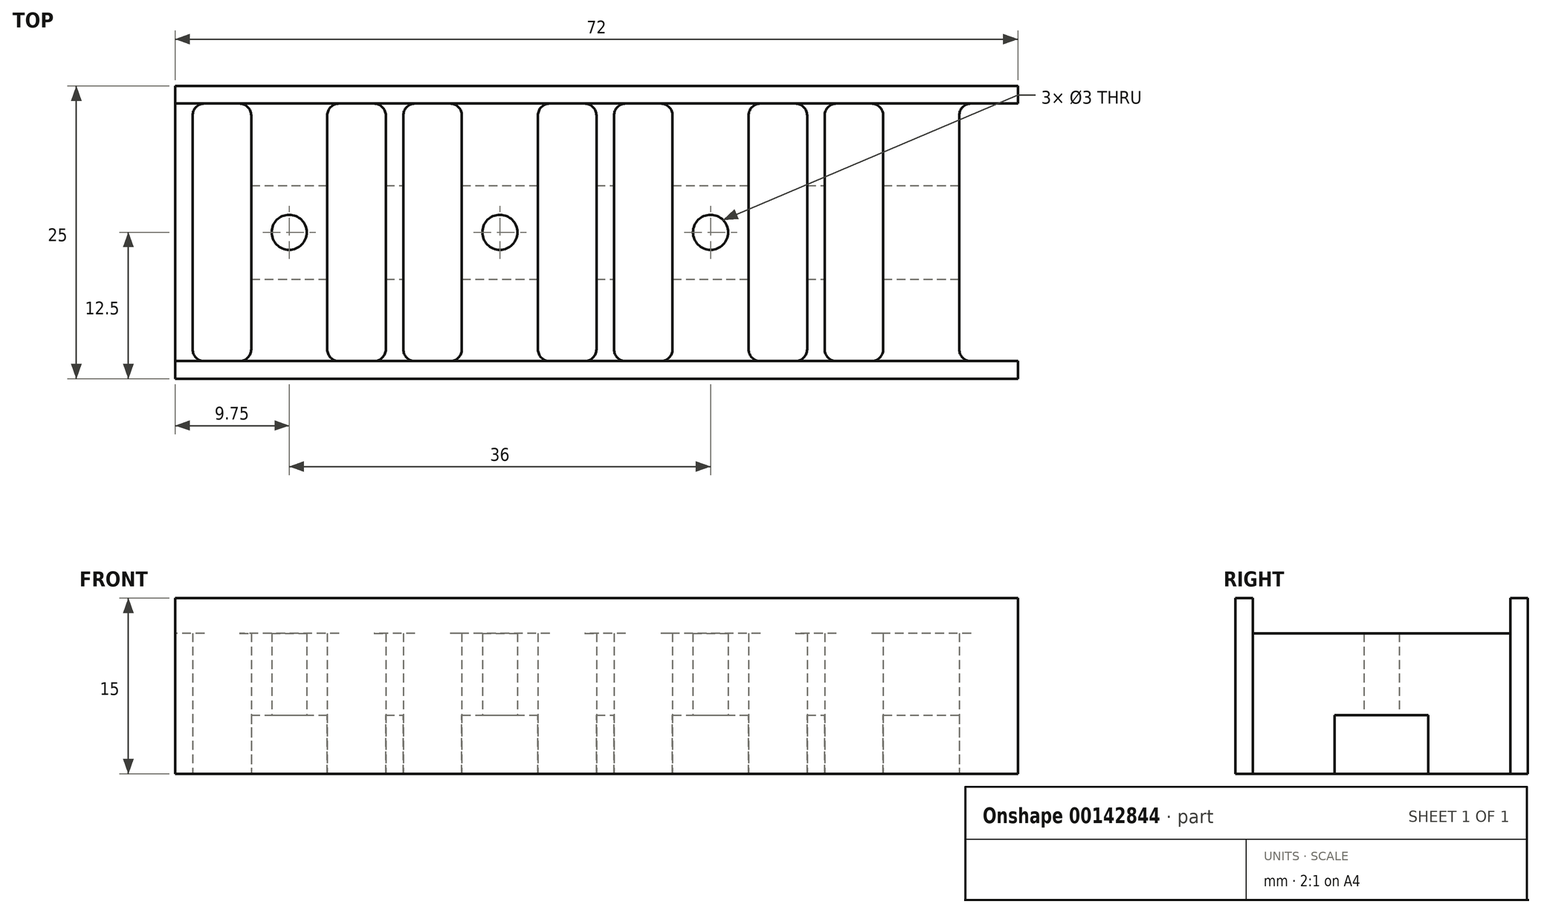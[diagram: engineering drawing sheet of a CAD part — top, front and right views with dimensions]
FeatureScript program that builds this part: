
annotation { "Feature Type Name" : "Feature", "Feature Type Description" : "" }
export const myFeature = defineFeature(function(context is Context, id is Id, definition is map)
    precondition{}
    {
        {
            var Q0;
            Q0=qCreatedBy(makeId("Top.planeOp"),FACE);
            var sketch = newSketch(context, id + "F0", { "sketchPlane" : qUnion([Q0])});
            skLineSegment(sketch, "E0.bottom", {"start": v(0, 12.5) * mm, "end": v(18, 12.5) * mm});
            skLineSegment(sketch, "E0.top", {"start": v(0, -12.5) * mm, "end": v(18, -12.5) * mm});
            skLineSegment(sketch, "E0.left", {"start": v(0, 12.5) * mm, "end": v(0, -12.5) * mm});
            skLineSegment(sketch, "E0.right", {"start": v(18, 12.5) * mm, "end": v(18, 11) * mm});
            skLineSegment(sketch, "E1.bottom", {"start": v(14, 11) * mm, "end": v(18, 11) * mm});
            skLineSegment(sketch, "E1.top", {"start": v(14, -11) * mm, "end": v(18, -11) * mm});
            skLineSegment(sketch, "E1.left", {"start": v(13, 10) * mm, "end": v(13, -10) * mm});
            skLineSegment(sketch, "E2.trimOffspring", {"start": v(18, -11) * mm, "end": v(18, -12.5) * mm});
            skLineSegment(sketch, "E3.bottom", {"start": v(2.5, 11) * mm, "end": v(5.5, 11) * mm});
            skLineSegment(sketch, "E3.top", {"start": v(2.5, -11) * mm, "end": v(5.5, -11) * mm});
            skLineSegment(sketch, "E3.left", {"start": v(1.5, 10) * mm, "end": v(1.5, -10) * mm});
            skLineSegment(sketch, "E3.right", {"start": v(6.5, 10) * mm, "end": v(6.5, -10) * mm});
            skCircle(sketch, "E4", {"center": v(9.75, 0) * mm, "radius": 1.5 * mm});
            skPoint(sketch, "E5.visualSharp", {"position": v(7.25, 11) * mm});
            skPoint(sketch, "E6.visualSharp", {"position": v(12.25, 11) * mm});
            skPoint(sketch, "E7.visualSharp", {"position": v(12.25, 3) * mm});
            skPoint(sketch, "E8.visualSharp", {"position": v(7.25, 3) * mm});
            skPoint(sketch, "E9.visualSharp", {"position": v(7.25, -3) * mm});
            skPoint(sketch, "E10.visualSharp", {"position": v(7.25, -11) * mm});
            skPoint(sketch, "E11.visualSharp", {"position": v(12.25, -11) * mm});
            skPoint(sketch, "E12.visualSharp", {"position": v(12.25, -3) * mm});
            skPoint(sketch, "E13.visualSharp", {"position": v(13, 11) * mm});
            skArc(sketch, "E13.filletArc", {"start": v(14, 11) * mm, "mid": v(13.3, 10.7) * mm, "end": v(13, 10) * mm});
            skPoint(sketch, "E14.visualSharp", {"position": v(13, -11) * mm});
            skArc(sketch, "E14.filletArc", {"start": v(13, -10) * mm, "mid": v(13.3, -10.7) * mm, "end": v(14, -11) * mm});
            skPoint(sketch, "E15.visualSharp", {"position": v(6.5, 11) * mm});
            skArc(sketch, "E15.filletArc", {"start": v(6.5, 10) * mm, "mid": v(6.2, 10.7) * mm, "end": v(5.5, 11) * mm});
            skPoint(sketch, "E16.visualSharp", {"position": v(6.5, -11) * mm});
            skArc(sketch, "E16.filletArc", {"start": v(5.5, -11) * mm, "mid": v(6.2, -10.7) * mm, "end": v(6.5, -10) * mm});
            skPoint(sketch, "E17.visualSharp", {"position": v(1.5, 11) * mm});
            skArc(sketch, "E17.filletArc", {"start": v(2.5, 11) * mm, "mid": v(1.8, 10.7) * mm, "end": v(1.5, 10) * mm});
            skPoint(sketch, "E18.visualSharp", {"position": v(1.5, -11) * mm});
            skArc(sketch, "E18.filletArc", {"start": v(1.5, -10) * mm, "mid": v(1.8, -10.7) * mm, "end": v(2.5, -11) * mm});
            skPoint(sketch, "E19.1.0.0", {"position": v(30.25, 3) * mm});
            skPoint(sketch, "E19.1.0.1", {"position": v(24.5, 11) * mm});
            skPoint(sketch, "E19.1.0.3", {"position": v(25.25, -11) * mm});
            skPoint(sketch, "E19.1.0.4", {"position": v(19.5, -11) * mm});
            skPoint(sketch, "E19.1.0.6", {"position": v(30.25, -11) * mm});
            skPoint(sketch, "E19.1.0.7", {"position": v(31, 11) * mm});
            skPoint(sketch, "E19.1.0.8", {"position": v(25.25, 11) * mm});
            skPoint(sketch, "E19.1.0.9", {"position": v(30.25, 11) * mm});
            skPoint(sketch, "E19.1.0.10", {"position": v(31, -11) * mm});
            skPoint(sketch, "E19.1.0.12", {"position": v(25.25, 3) * mm});
            skPoint(sketch, "E19.1.0.13", {"position": v(24.5, -11) * mm});
            skCircle(sketch, "E19.1.0.15", {"center": v(27.75, 0) * mm, "radius": 1.5 * mm});
            skLineSegment(sketch, "E19.1.0.16", {"start": v(24.5, 10) * mm, "end": v(24.5, -10) * mm});
            skLineSegment(sketch, "E19.1.0.17", {"start": v(19.5, 10) * mm, "end": v(19.5, -10) * mm});
            skLineSegment(sketch, "E19.1.0.18", {"start": v(20.5, -11) * mm, "end": v(23.5, -11) * mm});
            skLineSegment(sketch, "E19.1.0.19", {"start": v(20.5, 11) * mm, "end": v(23.5, 11) * mm});
            skLineSegment(sketch, "E19.1.0.20", {"start": v(31, 10) * mm, "end": v(31, -10) * mm});
            skLineSegment(sketch, "E19.1.0.21", {"start": v(32, -11) * mm, "end": v(36, -11) * mm});
            skLineSegment(sketch, "E19.1.0.22", {"start": v(32, 11) * mm, "end": v(36, 11) * mm});
            skPoint(sketch, "E19.1.0.23", {"position": v(25.25, -3) * mm});
            skPoint(sketch, "E19.1.0.24", {"position": v(19.5, 11) * mm});
            skLineSegment(sketch, "E19.1.0.25", {"start": v(18, 12.5) * mm, "end": v(18, -12.5) * mm});
            skLineSegment(sketch, "E19.1.0.26", {"start": v(18, -12.5) * mm, "end": v(36, -12.5) * mm});
            skLineSegment(sketch, "E19.1.0.27", {"start": v(18, 12.5) * mm, "end": v(36, 12.5) * mm});
            skPoint(sketch, "E19.1.0.32", {"position": v(30.25, -3) * mm});
            skArc(sketch, "E19.1.0.33", {"start": v(19.5, -10) * mm, "mid": v(19.8, -10.7) * mm, "end": v(20.5, -11) * mm});
            skArc(sketch, "E19.1.0.37", {"start": v(23.5, -11) * mm, "mid": v(24.2, -10.7) * mm, "end": v(24.5, -10) * mm});
            skArc(sketch, "E19.1.0.40", {"start": v(24.5, 10) * mm, "mid": v(24.2, 10.7) * mm, "end": v(23.5, 11) * mm});
            skArc(sketch, "E19.1.0.42", {"start": v(20.5, 11) * mm, "mid": v(19.8, 10.7) * mm, "end": v(19.5, 10) * mm});
            skArc(sketch, "E19.1.0.43", {"start": v(31, -10) * mm, "mid": v(31.3, -10.7) * mm, "end": v(32, -11) * mm});
            skArc(sketch, "E19.1.0.45", {"start": v(32, 11) * mm, "mid": v(31.3, 10.7) * mm, "end": v(31, 10) * mm});
            skLineSegment(sketch, "E19.1.0.47", {"start": v(36, -11) * mm, "end": v(36, -12.5) * mm});
            skLineSegment(sketch, "E19.1.0.48", {"start": v(36, 12.5) * mm, "end": v(36, 11) * mm});
            skPoint(sketch, "E19.2.0.0", {"position": v(48.25, 3) * mm});
            skPoint(sketch, "E19.2.0.1", {"position": v(42.5, 11) * mm});
            skPoint(sketch, "E19.2.0.3", {"position": v(43.25, -11) * mm});
            skPoint(sketch, "E19.2.0.4", {"position": v(37.5, -11) * mm});
            skPoint(sketch, "E19.2.0.6", {"position": v(48.25, -11) * mm});
            skPoint(sketch, "E19.2.0.7", {"position": v(49, 11) * mm});
            skPoint(sketch, "E19.2.0.8", {"position": v(43.25, 11) * mm});
            skPoint(sketch, "E19.2.0.9", {"position": v(48.25, 11) * mm});
            skPoint(sketch, "E19.2.0.10", {"position": v(49, -11) * mm});
            skPoint(sketch, "E19.2.0.12", {"position": v(43.25, 3) * mm});
            skPoint(sketch, "E19.2.0.13", {"position": v(42.5, -11) * mm});
            skCircle(sketch, "E19.2.0.15", {"center": v(45.75, 0) * mm, "radius": 1.5 * mm});
            skLineSegment(sketch, "E19.2.0.16", {"start": v(42.5, 10) * mm, "end": v(42.5, -10) * mm});
            skLineSegment(sketch, "E19.2.0.17", {"start": v(37.5, 10) * mm, "end": v(37.5, -10) * mm});
            skLineSegment(sketch, "E19.2.0.18", {"start": v(38.5, -11) * mm, "end": v(41.5, -11) * mm});
            skLineSegment(sketch, "E19.2.0.19", {"start": v(38.5, 11) * mm, "end": v(41.5, 11) * mm});
            skLineSegment(sketch, "E19.2.0.20", {"start": v(49, 10) * mm, "end": v(49, -10) * mm});
            skLineSegment(sketch, "E19.2.0.21", {"start": v(50, -11) * mm, "end": v(54, -11) * mm});
            skLineSegment(sketch, "E19.2.0.22", {"start": v(50, 11) * mm, "end": v(54, 11) * mm});
            skPoint(sketch, "E19.2.0.23", {"position": v(43.25, -3) * mm});
            skPoint(sketch, "E19.2.0.24", {"position": v(37.5, 11) * mm});
            skLineSegment(sketch, "E19.2.0.25", {"start": v(36, 12.5) * mm, "end": v(36, -12.5) * mm});
            skLineSegment(sketch, "E19.2.0.26", {"start": v(36, -12.5) * mm, "end": v(54, -12.5) * mm});
            skLineSegment(sketch, "E19.2.0.27", {"start": v(36, 12.5) * mm, "end": v(54, 12.5) * mm});
            skPoint(sketch, "E19.2.0.32", {"position": v(48.25, -3) * mm});
            skArc(sketch, "E19.2.0.33", {"start": v(37.5, -10) * mm, "mid": v(37.8, -10.7) * mm, "end": v(38.5, -11) * mm});
            skArc(sketch, "E19.2.0.37", {"start": v(41.5, -11) * mm, "mid": v(42.2, -10.7) * mm, "end": v(42.5, -10) * mm});
            skArc(sketch, "E19.2.0.40", {"start": v(42.5, 10) * mm, "mid": v(42.2, 10.7) * mm, "end": v(41.5, 11) * mm});
            skArc(sketch, "E19.2.0.42", {"start": v(38.5, 11) * mm, "mid": v(37.8, 10.7) * mm, "end": v(37.5, 10) * mm});
            skArc(sketch, "E19.2.0.43", {"start": v(49, -10) * mm, "mid": v(49.3, -10.7) * mm, "end": v(50, -11) * mm});
            skArc(sketch, "E19.2.0.45", {"start": v(50, 11) * mm, "mid": v(49.3, 10.7) * mm, "end": v(49, 10) * mm});
            skLineSegment(sketch, "E19.2.0.47", {"start": v(54, -11) * mm, "end": v(54, -12.5) * mm});
            skLineSegment(sketch, "E19.2.0.48", {"start": v(54, 12.5) * mm, "end": v(54, 11) * mm});
            skPoint(sketch, "E19.3.0.0", {"position": v(66.25, 3) * mm});
            skPoint(sketch, "E19.3.0.1", {"position": v(60.5, 11) * mm});
            skPoint(sketch, "E19.3.0.3", {"position": v(61.25, -11) * mm});
            skPoint(sketch, "E19.3.0.4", {"position": v(55.5, -11) * mm});
            skPoint(sketch, "E19.3.0.6", {"position": v(66.25, -11) * mm});
            skPoint(sketch, "E19.3.0.7", {"position": v(67, 11) * mm});
            skPoint(sketch, "E19.3.0.8", {"position": v(61.25, 11) * mm});
            skPoint(sketch, "E19.3.0.9", {"position": v(66.25, 11) * mm});
            skPoint(sketch, "E19.3.0.10", {"position": v(67, -11) * mm});
            skPoint(sketch, "E19.3.0.12", {"position": v(61.25, 3) * mm});
            skPoint(sketch, "E19.3.0.13", {"position": v(60.5, -11) * mm});
            skLineSegment(sketch, "E19.3.0.16", {"start": v(60.5, 10) * mm, "end": v(60.5, -10) * mm});
            skLineSegment(sketch, "E19.3.0.17", {"start": v(55.5, 10) * mm, "end": v(55.5, -10) * mm});
            skLineSegment(sketch, "E19.3.0.18", {"start": v(56.5, -11) * mm, "end": v(59.5, -11) * mm});
            skLineSegment(sketch, "E19.3.0.19", {"start": v(56.5, 11) * mm, "end": v(59.5, 11) * mm});
            skLineSegment(sketch, "E19.3.0.20", {"start": v(67, 10) * mm, "end": v(67, -10) * mm});
            skLineSegment(sketch, "E19.3.0.21", {"start": v(68, -11) * mm, "end": v(72, -11) * mm});
            skLineSegment(sketch, "E19.3.0.22", {"start": v(68, 11) * mm, "end": v(72, 11) * mm});
            skPoint(sketch, "E19.3.0.23", {"position": v(61.25, -3) * mm});
            skPoint(sketch, "E19.3.0.24", {"position": v(55.5, 11) * mm});
            skLineSegment(sketch, "E19.3.0.25", {"start": v(54, 12.5) * mm, "end": v(54, -12.5) * mm});
            skLineSegment(sketch, "E19.3.0.26", {"start": v(54, -12.5) * mm, "end": v(72, -12.5) * mm});
            skLineSegment(sketch, "E19.3.0.27", {"start": v(54, 12.5) * mm, "end": v(72, 12.5) * mm});
            skPoint(sketch, "E19.3.0.32", {"position": v(66.25, -3) * mm});
            skArc(sketch, "E19.3.0.33", {"start": v(55.5, -10) * mm, "mid": v(55.8, -10.7) * mm, "end": v(56.5, -11) * mm});
            skArc(sketch, "E19.3.0.37", {"start": v(59.5, -11) * mm, "mid": v(60.2, -10.7) * mm, "end": v(60.5, -10) * mm});
            skArc(sketch, "E19.3.0.40", {"start": v(60.5, 10) * mm, "mid": v(60.2, 10.7) * mm, "end": v(59.5, 11) * mm});
            skArc(sketch, "E19.3.0.42", {"start": v(56.5, 11) * mm, "mid": v(55.8, 10.7) * mm, "end": v(55.5, 10) * mm});
            skArc(sketch, "E19.3.0.43", {"start": v(67, -10) * mm, "mid": v(67.3, -10.7) * mm, "end": v(68, -11) * mm});
            skArc(sketch, "E19.3.0.45", {"start": v(68, 11) * mm, "mid": v(67.3, 10.7) * mm, "end": v(67, 10) * mm});
            skLineSegment(sketch, "E19.3.0.47", {"start": v(72, -11) * mm, "end": v(72, -12.5) * mm});
            skLineSegment(sketch, "E19.3.0.48", {"start": v(72, 12.5) * mm, "end": v(72, 11) * mm});
            skLineSegment(sketch, "E19.direction1", {"start": v(0, -12.5) * mm, "end": v(18, -12.5) * mm, "construction": true});
            skSolve(sketch);
        }
        {
            var Q0;
            Q0 = qSketchRegion(id + "F0", true);
            extrude(context, id + "F1", {"entities" : qUnion([Q0]), "depth" : 15 * mm});
        }
        {
            var Q0;
            Q0=qCreatedBy(makeId("Top.planeOp"),FACE);
            var sketch = newSketch(context, id + "F2", { "sketchPlane" : qUnion([Q0])});
            skLineSegment(sketch, "E20.bottom", {"start": v(6.5, 4) * mm, "end": v(67, 4) * mm});
            skLineSegment(sketch, "E20.top", {"start": v(6.5, -4) * mm, "end": v(67, -4) * mm});
            skLineSegment(sketch, "E20.left", {"start": v(6.5, 4) * mm, "end": v(6.5, -4) * mm});
            skLineSegment(sketch, "E20.right", {"start": v(67, 4) * mm, "end": v(67, -4) * mm});
            skSolve(sketch);
        }
        {
            var Q0;
            Q0 = qSketchRegion(id + "F2", true);
            extrude(context, id + "F3", {"entities" : qUnion([Q0]), "operationType" : NewBodyOperationType.REMOVE, "depth" : 5 * mm});
        }
        {
            var Q0;
            Q0=makeQuery(id+"F1.opExtrude","SWEPT_FACE",FACE,{"disambiguationData":[OSD([sQuery(id+"F0.wireOp",EDGE,"E0.left")])]});
            var sketch = newSketch(context, id + "F4", { "sketchPlane" : qUnion([Q0])});
            skLineSegment(sketch, "E21.bottom", {"start": v(-11, 15) * mm, "end": v(11, 15) * mm});
            skLineSegment(sketch, "E21.top", {"start": v(-11, 12) * mm, "end": v(11, 12) * mm});
            skLineSegment(sketch, "E21.left", {"start": v(-11, 15) * mm, "end": v(-11, 12) * mm});
            skLineSegment(sketch, "E21.right", {"start": v(11, 15) * mm, "end": v(11, 12) * mm});
            skSolve(sketch);
        }
        {
            var Q0;
            Q0 = qSketchRegion(id + "F4", true);
            extrude(context, id + "F5", {"entities" : qUnion([Q0]), "operationType" : NewBodyOperationType.REMOVE, "oppositeDirection" : true, "depth" : 120 * mm});
        }
        {
            var Q0;
            Q0=makeQuery(id+"F1.opExtrude","SWEPT_EDGE",EDGE,{"disambiguationData":[OSD([sQuery(id+"F0.wireOp",EDGE,"E19.2.0.22"),sQuery(id+"F0.wireOp",EDGE,"E19.3.0.25")])]});
            var Q1;
            Q1=makeQuery(id+"F1.opExtrude","SWEPT_EDGE",EDGE,{"disambiguationData":[OSD([sQuery(id+"F0.wireOp",EDGE,"E19.1.0.22"),sQuery(id+"F0.wireOp",EDGE,"E19.2.0.25")])]});
            var Q2;
            Q2=makeQuery(id+"F1.opExtrude","SWEPT_EDGE",EDGE,{"disambiguationData":[OSD([sQuery(id+"F0.wireOp",EDGE,"E19.2.0.21"),sQuery(id+"F0.wireOp",EDGE,"E19.3.0.25")])]});
            var Q3;
            Q3=makeQuery(id+"F1.opExtrude","SWEPT_EDGE",EDGE,{"disambiguationData":[OSD([sQuery(id+"F0.wireOp",EDGE,"E19.1.0.21"),sQuery(id+"F0.wireOp",EDGE,"E19.2.0.25")])]});
            fillet(context, id + "F6", {"entities" : qUnion([Q0, Q1, Q2, Q3]), "radius" : 1 * mm, "tangentPropagation" : true, "allowEdgeOverflow" : false});
        }
        {
            var Q0;
            Q0=makeQuery(id+"F1.opExtrude","SWEPT_EDGE",EDGE,{"disambiguationData":[OSD([sQuery(id+"F0.wireOp",EDGE,"E1.bottom"),sQuery(id+"F0.wireOp",EDGE,"E19.1.0.25")])]});
            fillet(context, id + "F7", {"entities" : qUnion([Q0]), "radius" : 1 * mm, "tangentPropagation" : true, "allowEdgeOverflow" : false});
        }
        {
            var Q0;
            Q0=makeQuery(id+"F1.opExtrude","SWEPT_EDGE",EDGE,{"disambiguationData":[OSD([sQuery(id+"F0.wireOp",EDGE,"E1.top"),sQuery(id+"F0.wireOp",EDGE,"E19.1.0.25")])]});
            fillet(context, id + "F8", {"entities" : qUnion([Q0]), "radius" : 1 * mm, "tangentPropagation" : true, "allowEdgeOverflow" : false});
        }
    });
